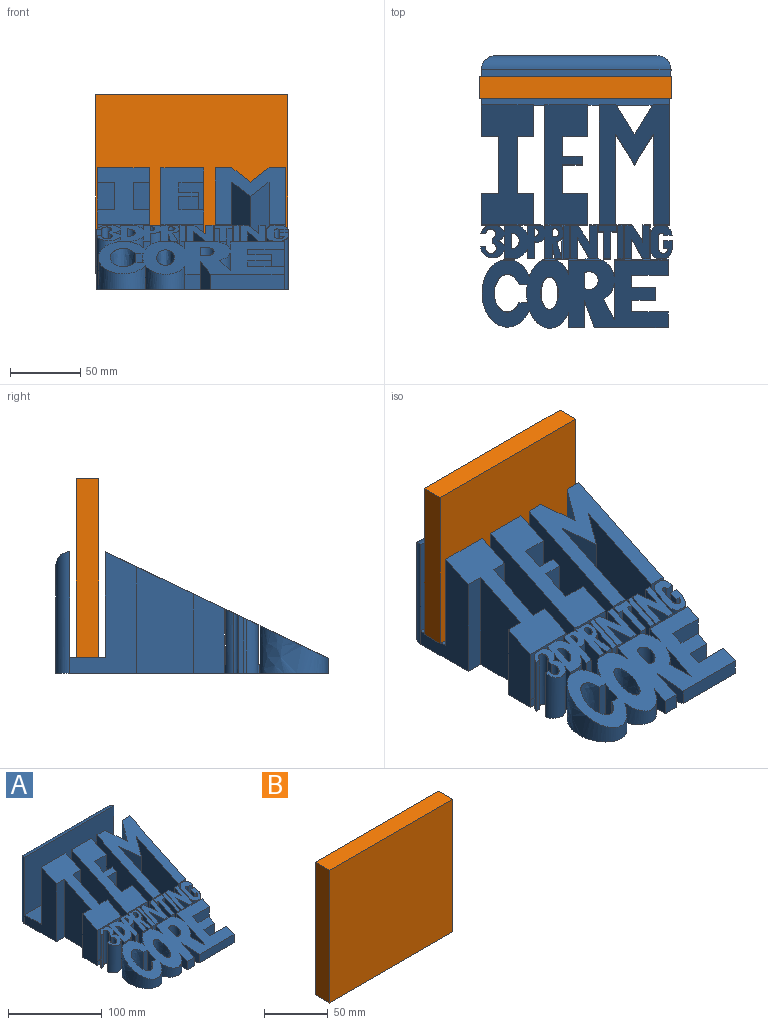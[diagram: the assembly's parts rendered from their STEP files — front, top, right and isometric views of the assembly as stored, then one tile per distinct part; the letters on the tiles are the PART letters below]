
ASSEMBLY  parts=2 mates=1
PART A: 222 faces, bbox 136.4x193.7x86.5 mm
  f0: plane 56.49x11.41mm, normal (0,1,0), area 644.5mm2, adj f99,f115,f217,f221
  f1: plane 75.67x11.41mm, normal (0,-1,0), area 863.3mm2, adj f99,f114,f217,f221
  f2: plane 40.45x5.57mm, normal (1,0,0), area 217.8mm2, adj f52,f60,f212,f221
  f3: plane 33.83x10.59mm, normal (-1,0,0), area 321.1mm2, adj f16,f138,f168,f201,f207,f221
  f4: plane 45.5x13.16mm, normal (0.83,0.55,0), area 649.9mm2, adj f25,f143,f174,f201,f213,f221
  f5: plane 45.5x4.96mm, normal (-1,0,0), area 201.2mm2, adj f11,f139,f155,f171,f209,f221
  f6: cylinder r=6.48mm len=45.5mm, axis (0,0,-1), area 574.2mm2, adj f81,f117,f140,f144,f173,f201,f209,f221
  f7: plane 87.72x86.42mm, normal (-1,0,0), area 5705.5mm2, adj f8,f147,f157,f173,f176,f201,f209,f215
  f8: cylinder r=6.48mm len=45.5mm, axis (0,0,-1), area 126.1mm2, adj f7,f153,f155,f172,f209,f221
  f9: plane 45.5x6.69mm, normal (-1,0,0), area 275.8mm2, adj f10,f141,f155,f172,f209,f221
  f10: cylinder r=12.44mm len=45.5mm, axis (0,0,-1), area 409.8mm2, adj f9,f141,f155,f171,f209,f221
  f11: cylinder r=8.9mm len=45.5mm, axis (0,0,-1), area 294.4mm2, adj f5,f139,f155,f170,f209,f221
  f12: cylinder r=8.9mm len=45.5mm, axis (0,0,-1), area 345.6mm2, adj f86,f142,f155,f170,f209,f221
  f13: cylinder r=7.84mm len=45.5mm, axis (0,0,-1), area 397.5mm2, adj f66,f135,f180,f202,f212,f221
  f14: cylinder r=7.84mm len=45.5mm, axis (0,0,-1), area 316.8mm2, adj f130,f136,f180,f185,f202,f203,f212,f221
  f15: extruded ~33.83x12.38mm, area 485.3mm2, adj f20,f67,f169,f201,f207,f221
  f16: extruded ~33.83x10.73mm, area 436.6mm2, adj f3,f133,f169,f201,f207,f221
  f17: cylinder r=15.75mm len=33.83mm, axis (0,0,-1), area 498.9mm2, adj f19,f51,f168,f201,f207,f221
  f18: plane 33.83x11.3mm, normal (1,0,0), area 340.8mm2, adj f42,f123,f195,f203,f207,f221
  f19: plane 33.83x12.14mm, normal (-1,0,0), area 364.5mm2, adj f17,f120,f195,f203,f207,f221
  f20: extruded ~47.91x33.83mm, area 2244.6mm2, adj f15,f43,f200,f206,f207,f221
  f21: plane 43.36x4.85mm, normal (0,-1,0), area 173.3mm2, adj f51,f54,f197,f203,f208,f221
  f22: cylinder r=7.84mm len=36.58mm, axis (0,0,-1), area 270.3mm2, adj f122,f129,f185,f186,f203,f212,f221
  f23: plane 45.5x12.22mm, normal (-1,0,0), area 499.8mm2, adj f24,f131,f184,f203,f210,f221
  f24: plane 45.5x12.22mm, normal (0.84,0.54,0), area 595.8mm2, adj f23,f132,f183,f203,f210,f221
  f25: plane 45.5x13.26mm, normal (-1,0,0), area 541.5mm2, adj f4,f118,f182,f203,f213,f221
  f26: extruded ~25.44x12.57mm, area 283.4mm2, adj f27,f49,f207,f221
  f27: plane 19.45x5.99mm, normal (0,1,0), area 116.4mm2, adj f26,f28,f207,f221
  f28: extruded ~29x26.8mm, area 1346.7mm2, adj f27,f49,f207,f221
  f29: cylinder r=15.75mm len=25.82mm, axis (0,0,-1), area 315.6mm2, adj f30,f46,f207,f221
  f30: plane 25.82x25.58mm, normal (-1,0,0), area 504.2mm2, adj f29,f46,f207,f221
  f31: cylinder r=6.45mm len=29.98mm, axis (0,0,-1), area 726.7mm2, adj f47,f207,f221
  f32: plane 20.02x19.16mm, normal (1,0,0), area 296mm2, adj f33,f48,f207,f221
  f33: plane 20.02x19.16mm, normal (-0.94,-0.34,0), area 315mm2, adj f32,f34,f207,f221
  f34: plane 52.5x10.88mm, normal (0,-1,0), area 571.2mm2, adj f33,f35,f207,f221
  f35: plane 16.28x11.3mm, normal (1,0,0), area 153.5mm2, adj f34,f36,f207,f221
  f36: plane 25.78x16.28mm, normal (0,1,0), area 419.6mm2, adj f35,f37,f207,f221
  f37: plane 20.26x8.35mm, normal (1,0,0), area 152.6mm2, adj f36,f38,f207,f221
  f38: plane 20.26x16.6mm, normal (0,-1,0), area 336.4mm2, adj f37,f39,f207,f221
  f39: plane 24.62x9.13mm, normal (1,0,0), area 204.9mm2, adj f38,f40,f207,f221
  f40: plane 24.62x16.6mm, normal (0,1,0), area 408.8mm2, adj f39,f41,f207,f221
  f41: plane 28.67x8.48mm, normal (1,0,0), area 226mm2, adj f40,f42,f207,f221
  f42: plane 28.67x25.78mm, normal (0,-1,0), area 739.1mm2, adj f18,f41,f207,f221
  f43: extruded ~28.12x16.89mm, area 511.1mm2, adj f20,f44,f207,f221
  f44: plane 16.2x11.14mm, normal (-1,0,0), area 150.8mm2, adj f43,f48,f207,f221
  f45: extruded ~28.09x23.03mm, area 1293.8mm2, adj f207,f221
  f46: plane 20.57x14.58mm, normal (0.89,0.46,0), area 280.5mm2, adj f29,f30,f207,f221
  f47: plane 29.55x11.17mm, normal (1,0,0), area 300.3mm2, adj f31,f207,f221
  f48: plane 11.04x10.88mm, normal (0,-1,0), area 120.1mm2, adj f32,f44,f207,f221
  f49: plane 25.44x5.65mm, normal (0,-1,0), area 143.7mm2, adj f26,f28,f207,f221
  f50: plane 41.34x14.74mm, normal (-0.87,-0.5,0), area 641.4mm2, adj f53,f124,f163,f201,f213,f221
  f51: plane 45.5x23.45mm, normal (1,0,0), area 905.8mm2, adj f17,f21,f163,f182,f201,f203,f213,f221
  f52: cylinder r=7.84mm len=37.79mm, axis (0,0,-1), area 349.6mm2, adj f2,f123,f186,f203,f212,f221
  f53: plane 41.34x15.24mm, normal (1,0,0), area 560.8mm2, adj f50,f125,f161,f201,f213,f221
  f54: plane 43.36x19.39mm, normal (-1,0,0), area 739.8mm2, adj f21,f126,f199,f205,f208,f221
  f55: plane 43.36x19.39mm, normal (1,0,0), area 739.8mm2, adj f56,f126,f199,f205,f208,f221
  f56: plane 43.36x4.67mm, normal (0,-1,0), area 175.1mm2, adj f55,f57,f196,f203,f208,f221
  f57: plane 45.5x23.8mm, normal (-1,0,0), area 909.3mm2, adj f56,f127,f189,f191,f203,f211,f221
  f58: plane 40.84x14.19mm, normal (1,0,0), area 517.5mm2, adj f59,f121,f188,f203,f210,f221
  f59: plane 40.84x14.19mm, normal (-0.87,-0.49,0), area 592.3mm2, adj f58,f121,f187,f203,f210,f221
  f60: plane 40.45x5.99mm, normal (0,1,0), area 242.2mm2, adj f2,f61,f212,f221
  f61: plane 40.45x5.57mm, normal (-1,0,0), area 217.8mm2, adj f60,f62,f212,f221
  f62: plane 37.79x3mm, normal (0,-1,0), area 113.5mm2, adj f61,f63,f212,f221
  f63: cylinder r=3.38mm len=37.79mm, axis (0,0,-1), area 394.9mm2, adj f62,f64,f212,f221
  f64: plane 42.26x9.52mm, normal (1,0,0), area 380.7mm2, adj f63,f65,f212,f221
  f65: cylinder r=1.93mm len=42.97mm, axis (0,0,-1), area 219.7mm2, adj f64,f66,f212,f221
  f66: plane 42.26x5.95mm, normal (0,-1,0), area 251.6mm2, adj f13,f65,f212,f221
  f67: plane 41.49x15.25mm, normal (-1,0,0), area 571.9mm2, adj f15,f78,f178,f201,f209,f221
  f68: plane 39x9.83mm, normal (1,0,0), area 359.2mm2, adj f69,f119,f178,f201,f209,f221
  f69: plane 39x10.22mm, normal (-0.98,-0.2,0), area 370.4mm2, adj f68,f119,f177,f201,f209,f221
  f70: plane 37.08x6.21mm, normal (-1,0,0), area 209.9mm2, adj f83,f134,f198,f204,f209,f221
  f71: plane 42.21x7.28mm, normal (-1,0,0), area 294.6mm2, adj f84,f85,f209,f221
  f72: plane 43x11.27mm, normal (1,0,0), area 454.5mm2, adj f82,f209,f221
  f73: plane 44.51x5.72mm, normal (1,0,0), area 246.8mm2, adj f79,f209,f221
  f74: plane 44.06x4.02mm, normal (1,0,0), area 173.2mm2, adj f80,f209,f221
  f75: cylinder r=12.44mm len=37.56mm, axis (0,0,-1), area 412mm2, adj f76,f134,f198,f204,f209,f221
  f76: plane 37.56x6.82mm, normal (-1,0,0), area 245.1mm2, adj f75,f116,f209,f221
  f77: plane 40.05x12.04mm, normal (1,0,0), area 447.7mm2, adj f78,f116,f209,f221
  f78: cylinder r=6.48mm len=41.49mm, axis (0,0,-1), area 350.2mm2, adj f67,f77,f209,f221
  f79: cylinder r=2.86mm len=44.51mm, axis (0,0,-1), area 387.7mm2, adj f73,f209,f221
  f80: cylinder r=2.87mm len=44.48mm, axis (0,0,-1), area 585.4mm2, adj f74,f209,f221
  f81: plane 40.01x11.17mm, normal (0.95,0.3,0), area 437.3mm2, adj f6,f117,f175,f209,f221
  f82: cylinder r=5.64mm len=43mm, axis (0,0,-1), area 704.2mm2, adj f72,f209,f221
  f83: cylinder r=8.91mm len=38.34mm, axis (0,0,-1), area 825mm2, adj f70,f90,f209,f221
  f84: cylinder r=7.35mm len=40.35mm, axis (0,0,-1), area 229.2mm2, adj f71,f85,f209,f221
  f85: cylinder r=7.35mm len=42.21mm, axis (0,0,-1), area 252.3mm2, adj f71,f84,f209,f221
  f86: plane 42.84x3.57mm, normal (0,-1,0), area 152.9mm2, adj f12,f87,f209,f221
  f87: cylinder r=3.44mm len=44.39mm, axis (0,0,-1), area 623.3mm2, adj f86,f88,f209,f221
  f88: plane 41.27x3.57mm, normal (-1,0,0), area 144.3mm2, adj f87,f89,f209,f221
  f89: cylinder r=3.8mm len=39.57mm, axis (0,0,-1), area 655.8mm2, adj f88,f90,f209,f221
  f90: plane 38.34x3.85mm, normal (0,1,0), area 147.7mm2, adj f83,f89,f209,f221
  f91: plane 86.42x85.13mm, normal (-1,0,0), area 5612.1mm2, adj f118,f145,f158,f181,f203,f214,f221
  f92: plane 76.25x63.82mm, normal (1,0,0), area 3878.9mm2, adj f93,f132,f181,f203,f214,f221
  f93: plane 76.25x21.31mm, normal (-0.85,-0.53,0), area 1783.7mm2, adj f92,f94,f214,f221
  f94: plane 76.25x21.31mm, normal (0.85,-0.53,0), area 1783.7mm2, adj f93,f95,f214,f221
  f95: plane 76.25x63.93mm, normal (-1,0,0), area 3879.6mm2, adj f94,f136,f179,f202,f214,f221
  f96: plane 86.42x85.24mm, normal (1,0,0), area 5612.8mm2, adj f135,f149,f159,f179,f202,f214,f221
  f97: plane 86.42x21.31mm, normal (-0.85,0.53,0), area 2038.6mm2, adj f98,f146,f159,f214,f221
  f98: plane 86.42x21.31mm, normal (0.85,0.53,0), area 2038.6mm2, adj f97,f146,f158,f214,f221
  f99: plane 75.67x40.17mm, normal (1,0,0), area 2654.6mm2, adj f0,f1,f217,f221
  f100: plane 86.42x22.31mm, normal (1,0,0), area 1809.5mm2, adj f113,f145,f157,f215,f221
  f101: plane 86.42x47.53mm, normal (-1,0,0), area 2112.2mm2, adj f102,f152,f156,f217,f218,f221
  f102: plane 75.67x12.41mm, normal (0,-1,0), area 939mm2, adj f101,f103,f217,f221
  f103: plane 75.67x40.17mm, normal (-1,0,0), area 2654.6mm2, adj f102,f104,f217,f221
  f104: plane 56.49x12.41mm, normal (0,1,0), area 701mm2, adj f103,f105,f217,f221
  f105: plane 56.49x22.53mm, normal (-1,0,0), area 1132.1mm2, adj f104,f142,f155,f160,f217,f221
  f106: plane 56.49x22.53mm, normal (1,0,0), area 1132.1mm2, adj f107,f143,f176,f201,f215,f221
  f107: plane 56.49x17.66mm, normal (0,1,0), area 997.6mm2, adj f106,f108,f215,f221
  f108: plane 66.08x20.09mm, normal (1,0,0), area 1231mm2, adj f107,f109,f215,f221
  f109: plane 66.08x13.6mm, normal (0,-1,0), area 898.8mm2, adj f108,f110,f215,f221
  f110: plane 69.03x6.18mm, normal (1,0,0), area 417.4mm2, adj f109,f111,f215,f221
  f111: plane 69.03x13.6mm, normal (0,1,0), area 938.9mm2, adj f110,f112,f215,f221
  f112: plane 75.77x14.13mm, normal (1,0,0), area 1022.8mm2, adj f111,f113,f215,f221
  f113: plane 75.77x17.66mm, normal (0,-1,0), area 1338.1mm2, adj f100,f112,f215,f221
  f114: plane 86.42x22.53mm, normal (1,0,0), area 1826.2mm2, adj f1,f147,f156,f217,f221
  f115: plane 56.49x22.03mm, normal (1,0,0), area 1128.8mm2, adj f0,f154,f160,f217,f221
  f116: plane 34.3x5.08mm, normal (0,-1,0), area 174.3mm2, adj f76,f77,f209,f221
  f117: plane 13.34x6.44mm, normal (-1,0,0), area 85.9mm2, adj f6,f81,f201,f221
  f118: plane 6.81x6.44mm, normal (0,1,0), area 43.9mm2, adj f25,f91,f203,f221
  f119: extruded ~6.44x2.1mm, area 14mm2, adj f68,f69,f201,f221
  f120: plane 7.41x6.44mm, normal (0,1,0), area 47.7mm2, adj f19,f128,f203,f221
  f121: plane 7.9x6.44mm, normal (0,1,0), area 50.9mm2, adj f58,f59,f203,f221
  f122: plane 7.03x6.44mm, normal (0,1,0), area 45.2mm2, adj f22,f129,f203,f221
  f123: plane 6.44x4.14mm, normal (0,1,0), area 26.7mm2, adj f18,f52,f203,f221
  f124: cylinder r=15.75mm len=6.44mm, axis (0,0,-1), area 22mm2, adj f50,f125,f201,f221
  f125: plane 6.44x5.02mm, normal (0,1,0), area 32.3mm2, adj f53,f124,f201,f221
  f126: plane 6.44x5.08mm, normal (0,-1,0), area 32.7mm2, adj f54,f55,f205,f221
  f127: plane 6.44x5.08mm, normal (0,-1,0), area 32.7mm2, adj f57,f128,f203,f221
  f128: plane 6.44x0.15mm, normal (-1,0,0), area 1mm2, adj f120,f127,f203,f221
  f129: plane 7.8x6.44mm, normal (1,0,0), area 50.2mm2, adj f22,f122,f203,f221
  f130: plane 7.24x6.44mm, normal (1,0,0), area 46.6mm2, adj f14,f131,f203,f221
  f131: plane 6.44x5.08mm, normal (0,1,0), area 32.7mm2, adj f23,f130,f203,f221
  f132: plane 11.34x6.44mm, normal (0,1,0), area 73mm2, adj f24,f92,f203,f221
  f133: plane 6.44x4.68mm, normal (0,-1,0), area 30.1mm2, adj f16,f137,f201,f221
  f134: plane 6.44x5.08mm, normal (0,-1,0), area 32.7mm2, adj f70,f75,f204,f221
  f135: plane 6.44x4.61mm, normal (0,-1,0), area 29.7mm2, adj f13,f96,f202,f221
  f136: plane 6.44x4.47mm, normal (0,-1,0), area 28.8mm2, adj f14,f95,f202,f221
  f137: plane 6.44x0.14mm, normal (-1,0,0), area 0.9mm2, adj f133,f138,f201,f221
  f138: plane 6.44x5.18mm, normal (0,-1,0), area 33.4mm2, adj f3,f137,f201,f221
  f139: plane 6.44x5.76mm, normal (0,-1,0), area 37.1mm2, adj f5,f11,f155,f221
  f140: plane 6.44x1.88mm, normal (0,-1,0), area 12.1mm2, adj f6,f144,f201,f221
  f141: plane 7.7x6.44mm, normal (0,-1,0), area 49.6mm2, adj f9,f10,f155,f221
  f142: plane 6.44x5.74mm, normal (0,-1,0), area 36.9mm2, adj f12,f105,f155,f221
  f143: plane 7.28x6.44mm, normal (0,-1,0), area 46.9mm2, adj f4,f106,f201,f221
  f144: plane 6.44x1.55mm, normal (-1,0,0), area 10mm2, adj f6,f140,f201,f221
  f145: plane 11.44x8.3mm, normal (0,-1,0), area 95mm2, adj f91,f100,f218,f221
  f146: plane 26.39x11.44mm, normal (0,-1,0), area 301.9mm2, adj f97,f98,f218,f221
  f147: plane 11.44x8.3mm, normal (0,-1,0), area 95mm2, adj f7,f114,f218,f221
  f148: plane 11.44x0.01mm, normal (0,1,0), area 0.1mm2, adj f149,f151,f218,f221
  f149: plane 25x11.44mm, normal (1,-0.05,0), area 286.3mm2, adj f96,f148,f218,f221
  f150: plane 114.77x76.44mm, normal (0,1,0), area 8772.8mm2, adj f151,f152,f220,f221
  f151: cylinder r=10mm len=86.44mm, axis (0,0,-1), area 1300.7mm2, adj f148,f150,f219,f220,f221
  f152: cylinder r=10mm len=86.44mm, axis (0,0,1), area 1300.7mm2, adj f101,f150,f219,f220,f221
  f153: cylinder r=6.33mm len=6.44mm, axis (0,0,-1), area 8.5mm2, adj f8,f154,f155,f221
  f154: plane 6.44x4.55mm, normal (0,1,0), area 29.3mm2, adj f115,f153,f155,f221
  f155: plane 43.39x1mm, normal (0,0,1), area 34mm2, adj f5,f8,f9,f10,f11,f12,f105,f139
  f156: plane 74.98x36.84mm, normal (0,1,0), area 2762.6mm2, adj f101,f114,f217,f218
  f157: plane 74.98x30.44mm, normal (0,1,0), area 2282.3mm2, adj f7,f100,f215,f218
  f158: plane 74.98x11.69mm, normal (0,1,0), area 876.6mm2, adj f91,f98,f214,f218
  f159: plane 74.98x11.69mm, normal (0,1,0), area 876.6mm2, adj f96,f97,f214,f218
  f160: plane 39.54x36.84mm, normal (0,-1,0), area 1456.6mm2, adj f105,f115,f155,f217
  f161: plane 27.86x4.79mm, normal (0,-1,0), area 133.4mm2, adj f53,f164,f201,f213
  f162: plane 39.06x23.45mm, normal (-1,0,0), area 784.8mm2, adj f165,f167,f201,f216
  f163: plane 27.86x5.39mm, normal (0,-1,0), area 150.3mm2, adj f50,f51,f201,f213
  f164: plane 39.06x23.45mm, normal (-1,0,0), area 784.8mm2, adj f161,f174,f201,f213
  f165: plane 27.86x3.88mm, normal (0,-1,0), area 108.2mm2, adj f162,f166,f201,f216
  f166: plane 39.06x23.45mm, normal (1,0,0), area 784.8mm2, adj f165,f167,f201,f216
  f167: plane 39.06x3.88mm, normal (0,1,0), area 151.7mm2, adj f162,f166,f201,f216
  f168: plane 27.39x23.46mm, normal (0,1,0), area 642.6mm2, adj f3,f17,f201,f207
  f169: plane 27.39x10.53mm, normal (0,1,0), area 288.2mm2, adj f15,f16,f201,f207
  f170: plane 39.06x7.47mm, normal (0,1,0), area 291.6mm2, adj f11,f12,f155,f209
  f171: plane 39.06x10.04mm, normal (0,1,0), area 392mm2, adj f5,f10,f155,f209
  f172: plane 39.06x10.78mm, normal (0,1,0), area 421.2mm2, adj f8,f9,f155,f209
  f173: plane 39.06x10.78mm, normal (0,1,0), area 421.2mm2, adj f6,f7,f201,f209
  f174: plane 39.06x5.19mm, normal (0,1,0), area 202.8mm2, adj f4,f164,f201,f213
  f175: plane 28.24x0.78mm, normal (1,0,0), area 21.9mm2, adj f81,f177,f201,f209
  f176: plane 39.54x30.44mm, normal (0,-1,0), area 1203.4mm2, adj f7,f106,f201,f215
  f177: plane 27.86x4.79mm, normal (0,-1,0), area 133.4mm2, adj f69,f175,f201,f209
  f178: plane 27.86x5.08mm, normal (0,-1,0), area 141.5mm2, adj f67,f68,f201,f209
  f179: plane 39.54x11.69mm, normal (0,-1,0), area 462.2mm2, adj f95,f96,f202,f214
  f180: plane 39.06x6.06mm, normal (0,1,0), area 236.7mm2, adj f13,f14,f202,f212
  f181: plane 39.54x11.69mm, normal (0,-1,0), area 462.2mm2, adj f91,f92,f203,f214
  f182: plane 39.06x5.08mm, normal (0,1,0), area 198.4mm2, adj f25,f51,f203,f213
  f183: plane 39.06x5.38mm, normal (0,1,0), area 210.1mm2, adj f24,f193,f203,f210
  f184: plane 39.06x4.62mm, normal (0,1,0), area 180.3mm2, adj f23,f194,f203,f210
  f185: plane 36.85x14.06mm, normal (-1,0,0), area 470.8mm2, adj f14,f22,f203,f212
  f186: plane 27.86x5.73mm, normal (0,-1,0), area 159.7mm2, adj f22,f52,f203,f212
  f187: plane 27.86x4.92mm, normal (0,-1,0), area 137.1mm2, adj f59,f194,f203,f210
  f188: plane 27.86x4.98mm, normal (0,-1,0), area 138.8mm2, adj f58,f193,f203,f210
  f189: plane 27.86x3.98mm, normal (0,-1,0), area 110.8mm2, adj f57,f190,f203,f211
  f190: plane 39.06x23.45mm, normal (1,0,0), area 784.8mm2, adj f189,f191,f203,f211
  f191: plane 39.06x3.98mm, normal (0,1,0), area 155.3mm2, adj f57,f190,f203,f211
  f192: plane 39.06x12.85mm, normal (0,1,0), area 502.1mm2, adj f196,f197,f203,f208
  f193: plane 39.06x23.45mm, normal (-1,0,0), area 784.8mm2, adj f183,f188,f203,f210
  f194: plane 39.06x23.45mm, normal (1,0,0), area 784.8mm2, adj f184,f187,f203,f210
  f195: plane 38.3x27.39mm, normal (0,1,0), area 1048.9mm2, adj f18,f19,f203,f207
  f196: plane 39.06x4.47mm, normal (1,0,0), area 169.9mm2, adj f56,f192,f203,f208
  f197: plane 39.06x4.47mm, normal (-1,0,0), area 169.9mm2, adj f21,f192,f203,f208
  f198: plane 27.86x8.22mm, normal (0,-1,0), area 228.9mm2, adj f70,f75,f204,f209
  f199: plane 27.86x5.08mm, normal (0,-1,0), area 141.5mm2, adj f54,f55,f205,f208
  f200: plane 27.39x7.16mm, normal (0,1,0), area 196mm2, adj f20,f206,f207
  f201: plane 42.5x25.45mm, normal (0,0,1), area 109.9mm2, adj f3,f4,f6,f7,f15,f16,f17,f50
  f202: plane 11.69x1mm, normal (0,0,1), area 8.1mm2, adj f13,f14,f95,f96,f135,f136,f179,f180
  f203: plane 55.65x25.45mm, normal (0,0,1), area 106.1mm2, adj f14,f18,f19,f21,f22,f23,f24,f25
  f204: plane 8.22x0.4mm, normal (0,0,1), area 2.9mm2, adj f70,f75,f134,f198
  f205: plane 5.08x0.41mm, normal (0,0,1), area 2.1mm2, adj f54,f55,f126,f199
  f206: plane 7.16x0.48mm, normal (0,0,1), area 2.3mm2, adj f20,f200
  f207: plane 132.36x48.46mm, normal (0,-0.43,0.9), area 4879.9mm2, adj f3,f15,f16,f17,f18,f19,f20,f26
  f208: plane 23.45x12.85mm, normal (0,-0.43,0.9), area 170.5mm2, adj f21,f54,f55,f56,f192,f196,f197,f199
  f209: plane 59.33x23.54mm, normal (0,-0.43,0.9), area 1006.2mm2, adj f5,f6,f7,f8,f9,f10,f11,f12
  f210: plane 23.45x17.53mm, normal (0,-0.43,0.9), area 349.2mm2, adj f23,f24,f58,f59,f183,f184,f187,f188
  f211: plane 23.45x11.2mm, normal (0,-0.43,0.9), area 103.4mm2, adj f57,f189,f190,f191
  f212: plane 23.45x15.26mm, normal (0,-0.43,0.9), area 268.5mm2, adj f2,f13,f14,f22,f52,f60,f61,f62
  f213: plane 23.45x18.71mm, normal (0,-0.43,0.9), area 357.4mm2, adj f4,f25,f50,f51,f53,f161,f163,f164
  f214: plane 84.74x49.77mm, normal (0,-0.43,0.9), area 2818.4mm2, adj f91,f92,f93,f94,f95,f96,f97,f98
  f215: plane 84.74x40.45mm, normal (0,-0.43,0.9), area 2160.7mm2, adj f7,f100,f106,f107,f108,f109,f110,f111
  f216: plane 23.45x11.2mm, normal (0,-0.43,0.9), area 100.9mm2, adj f162,f165,f166,f167
  f217: plane 84.74x40.45mm, normal (0,-0.43,0.9), area 2399.1mm2, adj f0,f1,f99,f101,f102,f103,f104,f105
  f218: plane 134.78x25mm, normal (0,0,1), area 3355.4mm2, adj f101,f145,f146,f147,f148,f149,f156,f157
  f219: plane 134.77x75mm, normal (0,-1,0), area 10107.6mm2, adj f151,f152,f218,f220
  f220: cylinder r=10mm len=134.77mm, axis (-1,0,0), area 2002.8mm2, adj f150,f151,f152,f219
  f221: plane 193.57x136.32mm, normal (0,0,-1), area 18114.2mm2, adj f0,f1,f2,f3,f4,f5,f6,f7
PART B: 6 faces, bbox 136.5x15.9x127 mm
  f0: plane 136.53x15.88mm, normal (0,0,1), area 2167.3mm2, adj f1,f3,f4,f5
  f1: plane 127x15.88mm, normal (-1,0,0), area 2016.1mm2, adj f0,f2,f4,f5
  f2: plane 136.53x15.88mm, normal (0,0,-1), area 2167.3mm2, adj f1,f3,f4,f5
  f3: plane 127x15.88mm, normal (1,0,0), area 2016.1mm2, adj f0,f2,f4,f5
  f4: plane 136.53x127mm, normal (0,-1,0), area 17338.7mm2, adj f0,f1,f2,f3
  f5: plane 136.53x127mm, normal (0,1,0), area 17338.7mm2, adj f0,f1,f2,f3
PLACE A t=(-99.99,12.92,-25.42)mm
PLACE B t=(-438.04,-69.27,-17.74)mm
MATE fastened B.f2 <-> A.f218  axis (0,0,-1) through (-122.15,95.79,-0.42)mm
